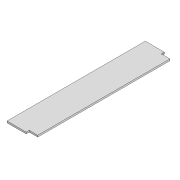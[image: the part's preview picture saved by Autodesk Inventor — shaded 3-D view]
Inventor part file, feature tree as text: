
AUTODESK INVENTOR PART (.ipt)
format: ipt  version: 2022 (Build 260153000, 153)  size: 108,032 bytes
history: native  units: mm
features: extrude x3, sketch x3, pattern_linear x1, plane x1, mirror x1
ambient origin geometry x8: Origin, YZ Plane, XZ Plane, XY Plane, X Axis, Y Axis, Z Axis, Center Point
bodies: Solid1 (feature_tree)
feature tree (9):
  extrude  "Extrusion1"  Depth=100.0mm
  extrude  "Extrusion2"  Depth=6.0mm
  pattern_linear  "Rectangular Pattern1"  Spacing1=10.0mm  [1 undecoded]
  plane  "Work Plane1"
  extrude  "Extrusion3"  Depth=31.0mm TaperAngle=0.0deg
  mirror  "Mirror1"
  sketch  "Sketch1"  dims[d0=500.0mm d1=100.0mm]
  sketch  "Sketch2"  dims[d2=6.0mm d3=0.0mm d4=2.95mm]
  sketch  "Sketch3"  dims[d5=5.0mm d6=10.0mm d7=10.0mm d8=0.0mm d9=30.0mm d11=6.0mm d12=11.0mm d13=31.0mm d14=10.0mm d15=0.0mm]
note: 1 required parameter value undecoded (feature->parameter linkage not recoverable at this tier; creation-order binding heuristic only, values carry confidence <= 0.55)
